# Revit family: L-industry NEW 12
name_source: partatom
category: Осветительные приборы
revit_build: Autodesk Revit 2017 (Build: 20160225_1515(x64)
units: mm (PartAtom-declared; Revit-internal decimal feet)

## family parameters
Источник света = Да
Общий = Нет
Основа = Грань
При загрузке вырезать с полостями = Нет
Размер круглого соединителя = Использовать диаметр
Тип детали = Нормальный
Точка расчета площади = Нет

## types (10) — shared parameters
Видимая форма излучения при визуализации = Нет
Изготовитель = LEDEL
Излучение по длине прямоугольника = 250 мм
Излучение по ширине прямоугольника = 67 мм
Изображение типоразмера = L-industry 12.png
Комментарии к типоразмеру = Бытовые
Отметка по умолчанию = 1219 мм
Полная установленная мощность = 11 В·А
Светофильтр = 16777215
Смещение цветовой температуры при затухании лампы = <Нет>
Угол наклона = 90.00°

## per-type parameters (varying)
| type | URL | Артикул | Группа модели | Описание | Файл фотометрической сетки |
| L-industry 12-11-D-5.0K |  | 504013 |  |  | L-industry NEW 12-11-D-5.0K-02.ies |
| L-industry 12-11-G60-5.0K |  | 504012 |  |  | L-industry NEW 12-11-G60-5.0K-01.ies |
| L-industry 12-11-K15-5.0K |  | 504010 |  |  | L-industry NEW 12-11-K15-5.0K-01.ies |
| L-industry 12-11-D-4.0K | https://ledel.ru | 204101300742200 | L-industry NEW 12 | Для освещения  промышленных объектов, складов, рекламных щитов, вывесок, декоративной подсветки | L-industry NEW 12-11-D-4.0K-02.ies |
| L-industry 12-11-K15-4.0K |  | 204101302741200 |  |  | L-industry NEW 12-11-K15-4.0K-01.ies |
| L-industry 12-11-G60-4.0K |  | 204101306741200 |  |  | L-industry NEW 12-11-G60-4.0K-01.ies |
| L-industry 12-11-G30-5.0K |  | 504011 |  |  | L-industry NEW 12-11-G30-5.0K-01.ies |
| L-industry 12-11-G30-4.0K |  | 204101304741200 |  |  | L-industry NEW 12-11-G30-4.0K-01.ies |
| L-industry 12-11-D-4.0K Duris |  | 204101300742200 |  |  | L-industry NEW 12-11-D-4.0K-02 Duris.ies |
| L-industry 12-11-D-5.0K Duris |  | 504013 |  |  | L-industry NEW 12-11-D-4.0K-02 Duris.ies |

## geometry (parser evidence)
native form markers: Sweep x3
no freeform markers — native parametric forms only
